# Revit family: PRD_FrankeWS_WCPans_HEAVY-DUTY_HDTX597
name_source: partatom
category: Plumbing Fixtures
revit_build: Autodesk Revit 2018 (Build: 20190510_1515(x64)
units: mm (PartAtom-declared; Revit-internal decimal feet)

## family parameters
Cut with Voids When Loaded = Yes
Host = Face
OmniClass Number = 23.45.05.21.11
OmniClass Title = Water Closets
Part Type = Normal
Room Calculation Point = No
Round Connector Dimension = Use Diameter
Shared = No

## types (1)
- HDTX597
    AssetType = Fixed
    BIMObjectName = PRD_AR_WCPans_CAMPUS_HDTX597
    Category = Pr_40_20_93_94, WC pans
    Default Elevation = 500 mm  [stored 1.64042 ft]
    Description = Campus floor standing WC pan for fitting through duct wall, manufactured from grade 1.4301 (304) stainless steel, material thickness 1.5mm for the pan and shroud - satin polish finish. The WC incorporates a stainless steel P trap 102mm o/d. A separate mounting plate and 4 bolts are provided for mounting the WC through a duct wall. The Campus WC has a pressed seating area that does not require a separate seat in vandal prone installations. However, a seat and lid can be fitted. Complies with BS EN 997 for 4.5 litre flushing. Also complies with the Australian and German test standards.
    DurationUnit = year
    Features = stainless steel, 1.50 mm, satin finished, bolt fix with duct wall, 360x400x500 mm (WxHxD)
    Finish = Satin finished
    Form = wall hung wc
    GrossWeight = 21.50 kg
    IfcExportAs = IfcSanitaryTerminalType
    IfcExportType = TOILETPAN
    InletSize = 55  [stored 0.180446 ft]
    Manufacturer = KWC Group AG
    ManufacturerName = KWC Group AG
    ManufacturerURL = www.kwc.com
    Material = PRD_AR_StainlessSteel_SatinFinished
    MaterialsBody = Stainless steel
    MaterialsFinishAndColour = Stainless steel
    MinimumFlushingCapacity = 4.00 L
    Model = HDTX597
    ModelNumber = 2000100729
    ModelReference = HDTX597
    NBSDescription = WC pans
    NBSReference = 45-35-70/384
    Name = CAMPUS WC HDTX597
    NetWeight = 19.10 kg
    NominalDepth = 400 mm  [stored 1.31234 ft]
    NominalHeight = 400 mm  [stored 1.31234 ft]
    NominalLength = 500 mm  [stored 1.64042 ft]
    NominalWidth = 360 mm  [stored 1.1811 ft]
    PanColor = Stainless steel
    PanHeight = 400
    PanMaterial = Stainless steel
    PanMounting = Floor standing
    ProductInformation = https://pim.kwc.com
    Size = 360 x 400 x 500 mm
    SpilloverLevel = 400 mm  [stored 1.31234 ft]
    ToiletPanType = Other
    ToiletType = LooseCoupled
    URL = www.kwc.com
    Uniclass2015Code = Pr_40_20_93_94
    Uniclass2015Title = WC pans
    Uniclass2015Version = Products v1.7
    Version = 1
    WarrantyDurationUnit = year
    WasteSize = 100  [stored 0.328084 ft]

note: [stored X ft] marks values corroborated as IEEE doubles in the binary element streams (Revit-internal decimal feet)

## geometry (parser evidence)
native form markers: Sweep x2
no freeform markers — native parametric forms only
